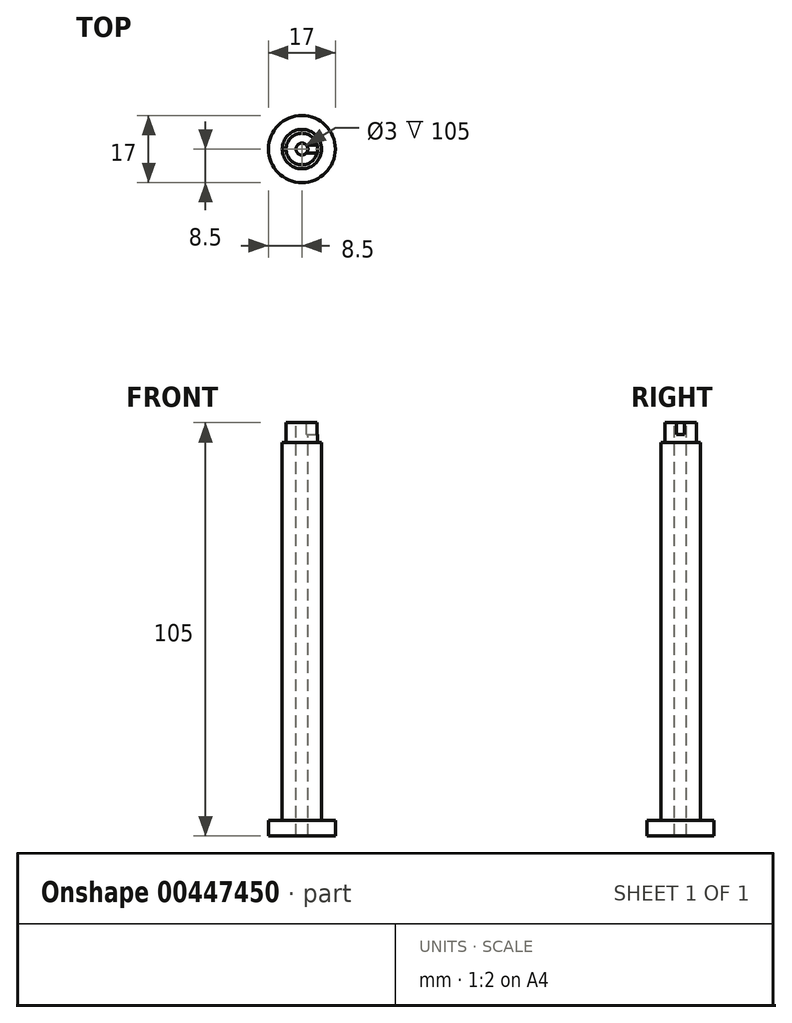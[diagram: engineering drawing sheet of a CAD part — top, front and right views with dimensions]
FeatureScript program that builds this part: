
annotation { "Feature Type Name" : "Feature", "Feature Type Description" : "" }
export const myFeature = defineFeature(function(context is Context, id is Id, definition is map)
    precondition{}
    {
        {
            var Q0;
            Q0=qCreatedBy(makeId("Top.planeOp"),FACE);
            var sketch = newSketch(context, id + "F0", { "sketchPlane" : qUnion([Q0])});
            skCircle(sketch, "E0", {"center": v(0, 0) * mm, "radius": 8.5 * mm});
            skSolve(sketch);
        }
        {
            var Q0;
            Q0=qSketchRegion(id+"F0",true);
            extrude(context, id + "F1", {"entities" : qUnion([Q0]), "depth" : 4 * mm});
        }
        {
            var Q0;
            Q0=qCreatedBy(makeId("Top.planeOp"),FACE);
            cPlane(context, id + "F2", {"entities" : qUnion([Q0]), "cplaneType" : CPlaneType.OFFSET, "offset" : 4 * mm, "width" : 150 * mm, "height" : 150 * mm});
        }
        {
            var Q0;
            Q0=qCreatedBy(makeId("Top.planeOp"),FACE);
            var sketch = newSketch(context, id + "F3", { "sketchPlane" : qUnion([Q0])});
            skCircle(sketch, "E1", {"center": v(0, 0) * mm, "radius": 5 * mm});
            skSolve(sketch);
        }
        {
            var Q0;
            Q0=qSketchRegion(id+"F3",true);
            extrude(context, id + "F4", {"entities" : qUnion([Q0]), "operationType" : NewBodyOperationType.ADD, "depth" : 100 * mm});
        }
        {
            var Q0;
            Q0=qCreatedBy(makeId("Right.planeOp"),FACE);
            var sketch = newSketch(context, id + "F5", { "sketchPlane" : qUnion([Q0])});
            skLineSegment(sketch, "E2.bottom", {"start": v(0, 105) * mm, "end": v(4, 105) * mm});
            skLineSegment(sketch, "E2.top", {"start": v(0, 100) * mm, "end": v(4, 100) * mm});
            skLineSegment(sketch, "E2.left", {"start": v(0, 105) * mm, "end": v(0, 100) * mm});
            skLineSegment(sketch, "E2.right", {"start": v(4, 105) * mm, "end": v(4, 100) * mm});
            skSolve(sketch);
        }
        {
            var Q0;
            Q0=makeQuery(id+"F5.imprint","IMPRINT",FACE,{"disambiguationData":[TD([[makeQuery(id+"F5.imprint","IMPRINT",EDGE,{"derivedFrom":sQuery(id+"F5.wireOp",EDGE,"E2.bottom")}),-1.0]])]});
            var Q1;
            Q1=sQuery(id+"F5.wireOp",EDGE,"E2.left");
            revolve(context, id + "F6", {"operationType" : NewBodyOperationType.ADD, "entities" : qUnion([Q0]), "axis" : qUnion([Q1]), "revolveType" : RevolveType.FULL});
        }
        {
            var Q0;
            Q0=qCreatedBy(id+"F2.planeOp",FACE);
            var sketch = newSketch(context, id + "F7", { "sketchPlane" : qUnion([Q0])});
            skLineSegment(sketch, "E3", {"start": v(8.44, 1) * mm, "end": v(8.44, -1) * mm});
            skSolve(sketch);
        }
        {
            var Q0;
            Q0=makeQuery(id+"F6.opRevolve","SWEPT_FACE",FACE,{"disambiguationData":[OSD([sQuery(id+"F5.wireOp",EDGE,"E2.bottom")])]});
            var sketch = newSketch(context, id + "F8", { "sketchPlane" : qUnion([Q0])});
            skLineSegment(sketch, "E4.bottom", {"start": v(1, 1) * mm, "end": v(5.32, 1) * mm});
            skLineSegment(sketch, "E4.top", {"start": v(1, -1) * mm, "end": v(5.32, -1) * mm});
            skLineSegment(sketch, "E4.left", {"start": v(1, 1) * mm, "end": v(1, -1) * mm});
            skLineSegment(sketch, "E4.right", {"start": v(5.32, 1) * mm, "end": v(5.32, -1) * mm});
            skSolve(sketch);
        }
        {
            var Q0;
            {var subQ0=sQuery(id+"F8.wireOp",EDGE,"E4.left");Q0=makeQuery(id+"F8.imprint","IMPRINT",FACE,{"disambiguationData":[TD([[makeQuery(id+"F8.imprint","IMPRINT",EDGE,{"derivedFrom":subQ0}),1.0]])]});}
            extrude(context, id + "F9", {"entities" : qUnion([Q0]), "operationType" : NewBodyOperationType.REMOVE, "oppositeDirection" : true, "depth" : 3 * mm});
        }
        {
            var Q0;
            Q0=makeQuery(id+"F6.opRevolve","SWEPT_FACE",FACE,{"disambiguationData":[OSD([sQuery(id+"F5.wireOp",EDGE,"E2.bottom")])]});
            var sketch = newSketch(context, id + "F10", { "sketchPlane" : qUnion([Q0])});
            skCircle(sketch, "E5", {"center": v(0, 0) * mm, "radius": 1.5 * mm});
            skSolve(sketch);
        }
        {
            var Q0;
            Q0 = qSketchRegion(id + "F10", true);
            extrude(context, id + "F11", {"entities" : qUnion([Q0]), "operationType" : NewBodyOperationType.REMOVE, "oppositeDirection" : true, "depth" : 118.9 * mm});
        }
    });
